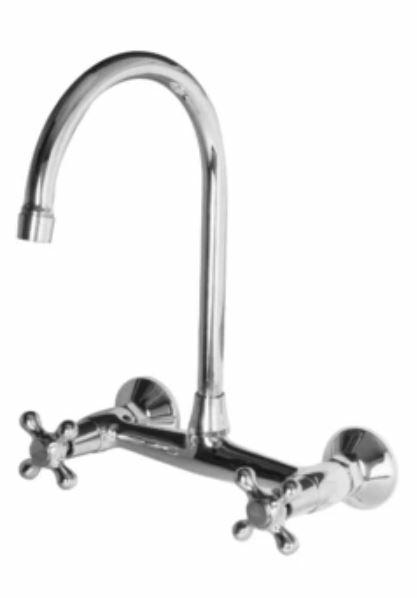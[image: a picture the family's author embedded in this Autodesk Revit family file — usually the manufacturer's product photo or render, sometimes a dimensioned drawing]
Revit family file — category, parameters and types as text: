
# Revit family: 01-0832-11-MEZCLADOR LAVAPLATOS PARED 8” ARCO CALIMA
name_source: partatom
category: Plumbing Fixtures
revit_build: Autodesk Revit 2018 (Build: 20170223_1515(x64)
units: mm (PartAtom-declared; Revit-internal decimal feet)

## family parameters
Cut with Voids When Loaded = No
Host = Face
OmniClass Number = 23.31.11.00
Part Type = Normal
Room Calculation Point = No
Round Connector Dimension = Use Diameter
Shared = No

## types (1)
- 01-0832-11
    Alto = 320.5 mm  [stored 1.05151 ft]
    Alto - aireador = 201.7 mm
    Ancho manija = 69 mm
    CW Connection = Yes
    Default Elevation = 0 mm  [stored 0 ft]
    Description = Bimando
    Eje - (roscas) = 203.2 mm
    Eje-Aireador = 186.4 mm
    HW Connection = Yes
    Link Ficha Tecnica = http://infotecnica.gricol.com
    Manufacturer = Gricol
    Metal Laton Cromado = Metal Laton Cromado
    Metal Zamak Cromado = Metal Zamak Cromado
    Model = 01-0832-11
    Plastico - ABS Cromado = Plastico - ABS Cromado
    Product Name = MEZCLADOR LAVAPLATOS PARED 8” ARCO CALIMA
    Type Image = MEZCLADOR LAVAPLATOS PARED 8” ARCO CALIMA.JPG
    URL = https://www.gricol.com
    Vent Connection = No
    Waste Connection = No

note: [stored X ft] marks values corroborated as IEEE doubles in the binary element streams (Revit-internal decimal feet)

## geometry (parser evidence)
native form markers: Blend x2, Sweep x5
no freeform markers — native parametric forms only
